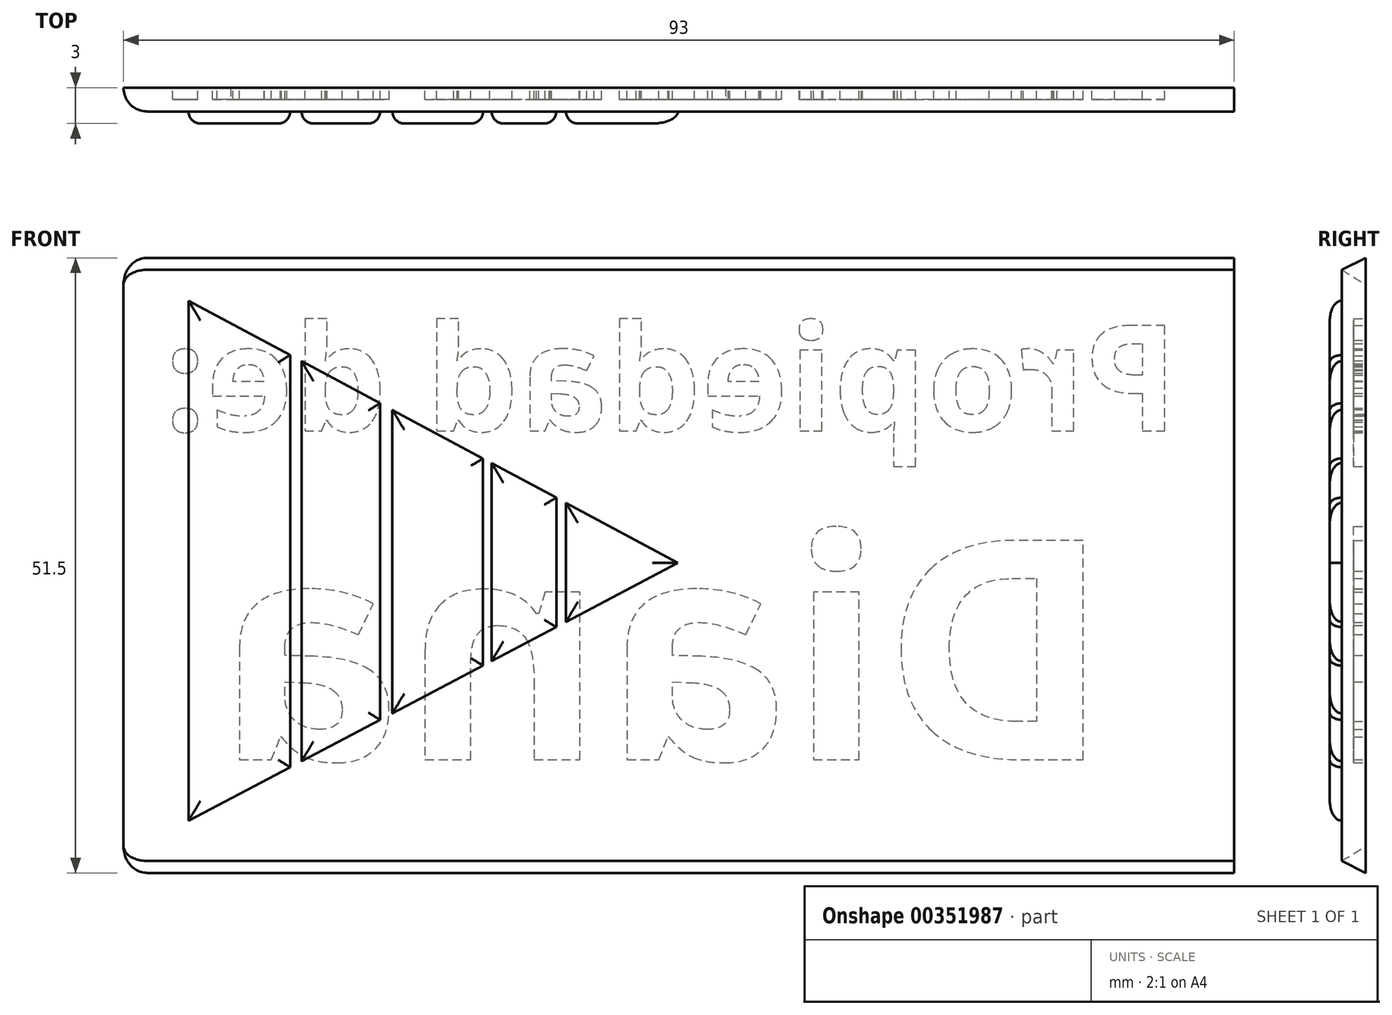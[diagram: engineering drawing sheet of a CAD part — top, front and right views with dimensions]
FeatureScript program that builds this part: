
annotation { "Feature Type Name" : "Feature", "Feature Type Description" : "" }
export const myFeature = defineFeature(function(context is Context, id is Id, definition is map)
    precondition{}
    {
        {
            var Q0;
            Q0=qCreatedBy(makeId("Front.planeOp"),FACE);
            var sketch = newSketch(context, id + "F0", { "sketchPlane" : qUnion([Q0])});
            skLineSegment(sketch, "E0", {"start": v(-25.75, -1) * mm, "end": v(25.75, -1) * mm});
            skLineSegment(sketch, "E1", {"start": v(-24.75, 1) * mm, "end": v(24.75, 1) * mm});
            skLineSegment(sketch, "E2", {"start": v(-24.75, 1) * mm, "end": v(-25.75, -1) * mm});
            skLineSegment(sketch, "E3", {"start": v(24.75, 1) * mm, "end": v(25.75, -1) * mm});
            skSolve(sketch);
        }
        {
            var Q0;
            Q0=makeQuery(id+"F0.imprint","IMPRINT",FACE,{"disambiguationData":[TD([[makeQuery(id+"F0.imprint","IMPRINT",EDGE,{"derivedFrom":sQuery(id+"F0.wireOp",EDGE,"E0")}),1.0]])]});
            extrude(context, id + "F1", {"entities" : qUnion([Q0]), "depth" : 93 * mm});
        }
        {
            var Q0;
            Q0=makeQuery(id+"F1.opExtrude","CAP_EDGE",EDGE,{"disambiguationData":[OSD([sQuery(id+"F0.wireOp",EDGE,"E1")])],"isStart":false});
            var Q1;
            Q1=makeQuery(id+"F1.opExtrude","CAP_EDGE",EDGE,{"disambiguationData":[OSD([sQuery(id+"F0.wireOp",EDGE,"E3")])],"isStart":false});
            var Q2;
            Q2=makeQuery(id+"F1.opExtrude","CAP_EDGE",EDGE,{"disambiguationData":[OSD([sQuery(id+"F0.wireOp",EDGE,"E2")])],"isStart":false});
            fillet(context, id + "F2", {"entities" : qUnion([Q0, Q1, Q2]), "radius" : 2 * mm, "tangentPropagation" : true, "allowEdgeOverflow" : false});
        }
        {
            var Q0;
            Q0=makeQuery(id+"F1.opExtrude","SWEPT_FACE",FACE,{"disambiguationData":[OSD([sQuery(id+"F0.wireOp",EDGE,"E1")])]});
            var sketch = newSketch(context, id + "F3", { "sketchPlane" : qUnion([Q0])});
            skLineSegment(sketch, "E4", {"start": v(-24.95, -92.76) * mm, "end": v(24.75, 0) * mm});
            skLineSegment(sketch, "E5", {"start": v(24.25, -93) * mm, "end": v(-24.75, 0) * mm});
            skLineSegment(sketch, "E6", {"start": v(-5.23, -55.95) * mm, "end": v(4.73, -55.95) * mm});
            skLineSegment(sketch, "E7", {"start": v(4.73, -55.95) * mm, "end": v(5.16, -56.76) * mm});
            skLineSegment(sketch, "E8", {"start": v(-5.67, -56.76) * mm, "end": v(5.16, -56.76) * mm});
            skLineSegment(sketch, "E9", {"start": v(-8.57, -62.18) * mm, "end": v(8.01, -62.18) * mm});
            skLineSegment(sketch, "E10", {"start": v(8.01, -62.18) * mm, "end": v(8.39, -62.9) * mm});
            skLineSegment(sketch, "E11", {"start": v(8.39, -62.9) * mm, "end": v(-8.95, -62.9) * mm});
            skLineSegment(sketch, "E12", {"start": v(-8.95, -62.9) * mm, "end": v(-13.02, -70.48) * mm});
            skLineSegment(sketch, "E13", {"start": v(-13.02, -70.48) * mm, "end": v(12.39, -70.48) * mm});
            skLineSegment(sketch, "E14", {"start": v(-13.57, -71.51) * mm, "end": v(12.93, -71.51) * mm});
            skLineSegment(sketch, "E15", {"start": v(16.4, -78.1) * mm, "end": v(-17.1, -78.1) * mm});
            skLineSegment(sketch, "E16", {"start": v(-17.6, -79.04) * mm, "end": v(16.9, -79.04) * mm});
            skLineSegment(sketch, "E17", {"start": v(-22.16, -87.55) * mm, "end": v(21.38, -87.55) * mm});
            skSolve(sketch);
        }
        {
            var Q0;
            {var subQ0=sQuery(id+"F3.wireOp",EDGE,"E6");Q0=makeQuery(id+"F3.imprint","IMPRINT",FACE,{"disambiguationData":[TD([[makeQuery(id+"F3.imprint","IMPRINT",EDGE,{"derivedFrom":subQ0}),1.0]])]});}
            var Q1;
            {var subQ0=sQuery(id+"F3.wireOp",EDGE,"E8");Q1=makeQuery(id+"F3.imprint","IMPRINT",FACE,{"disambiguationData":[TD([[makeQuery(id+"F3.imprint","IMPRINT",EDGE,{"derivedFrom":subQ0}),-1.0]])]});}
            var Q2;
            {var subQ0=sQuery(id+"F3.wireOp",EDGE,"E11");Q2=makeQuery(id+"F3.imprint","IMPRINT",FACE,{"disambiguationData":[TD([[makeQuery(id+"F3.imprint","IMPRINT",EDGE,{"derivedFrom":subQ0}),1.0]])]});}
            var Q3;
            {var subQ0=sQuery(id+"F3.wireOp",EDGE,"E14");Q3=makeQuery(id+"F3.imprint","IMPRINT",FACE,{"disambiguationData":[TD([[makeQuery(id+"F3.imprint","IMPRINT",EDGE,{"derivedFrom":subQ0}),-1.0]])]});}
            var Q4;
            {var subQ0=sQuery(id+"F3.wireOp",EDGE,"E16");Q4=makeQuery(id+"F3.imprint","IMPRINT",FACE,{"disambiguationData":[TD([[makeQuery(id+"F3.imprint","IMPRINT",EDGE,{"derivedFrom":subQ0}),-1.0]])]});}
            extrude(context, id + "F4", {"entities" : qUnion([Q0, Q1, Q2, Q3, Q4]), "operationType" : NewBodyOperationType.ADD, "depth" : 1 * mm});
        }
        {
            var Q0;
            Q0=makeQuery(id+"F4.opExtrude","CAP_FACE",FACE,{"disambiguationData":[OSD([sQuery(id+"F3.wireOp",EDGE,"E4"),sQuery(id+"F3.wireOp",EDGE,"E5"),sQuery(id+"F3.wireOp",EDGE,"E6")])],"isStart":false});
            var Q1;
            Q1=makeQuery(id+"F4.opExtrude","CAP_FACE",FACE,{"disambiguationData":[OSD([sQuery(id+"F3.wireOp",EDGE,"E4"),sQuery(id+"F3.wireOp",EDGE,"E5"),sQuery(id+"F3.wireOp",EDGE,"E8"),sQuery(id+"F3.wireOp",EDGE,"E9")])],"isStart":false});
            var Q2;
            Q2=makeQuery(id+"F4.opExtrude","CAP_FACE",FACE,{"disambiguationData":[OSD([sQuery(id+"F3.wireOp",EDGE,"E5"),sQuery(id+"F3.wireOp",EDGE,"E11"),sQuery(id+"F3.wireOp",EDGE,"E12"),sQuery(id+"F3.wireOp",EDGE,"E13")])],"isStart":false});
            var Q3;
            Q3=makeQuery(id+"F4.opExtrude","CAP_FACE",FACE,{"disambiguationData":[OSD([sQuery(id+"F3.wireOp",EDGE,"E4"),sQuery(id+"F3.wireOp",EDGE,"E5"),sQuery(id+"F3.wireOp",EDGE,"E16"),sQuery(id+"F3.wireOp",EDGE,"E17")])],"isStart":false});
            var Q4;
            Q4=makeQuery(id+"F4.opExtrude","CAP_FACE",FACE,{"disambiguationData":[OSD([sQuery(id+"F3.wireOp",EDGE,"E4"),sQuery(id+"F3.wireOp",EDGE,"E5"),sQuery(id+"F3.wireOp",EDGE,"E14"),sQuery(id+"F3.wireOp",EDGE,"E15")])],"isStart":false});
            fillet(context, id + "F5", {"entities" : qUnion([Q0, Q1, Q2, Q3, Q4]), "radius" : 1 * mm, "tangentPropagation" : true, "allowEdgeOverflow" : false});
        }
        {
            var Q0;
            Q0=makeQuery(id+"F1.opExtrude","SWEPT_BODY",BODY,{"disambiguationData":[OSD([sQuery(id+"F0.wireOp",EDGE,"E0"),sQuery(id+"F0.wireOp",EDGE,"E1"),sQuery(id+"F0.wireOp",EDGE,"E2"),sQuery(id+"F0.wireOp",EDGE,"E3")])]});
            var Q1;
            Q1=makeQuery(id+"F1.opExtrude","SWEPT_EDGE",EDGE,{"disambiguationData":[OSD([sQuery(id+"F0.wireOp",EDGE,"E0"),sQuery(id+"F0.wireOp",EDGE,"E2")])]});
            transform(context, id + "F6", {"entities" : qUnion([Q0]), "transformType" : TransformType.ROTATION, "transformAxis" : qUnion([Q1]), "angle" : 90 * degree, "makeCopy" : false});
        }
        {
            var Q0;
            Q0=makeQuery(id+"F1.opExtrude","SWEPT_BODY",BODY,{"disambiguationData":[OSD([sQuery(id+"F0.wireOp",EDGE,"E0"),sQuery(id+"F0.wireOp",EDGE,"E1"),sQuery(id+"F0.wireOp",EDGE,"E2"),sQuery(id+"F0.wireOp",EDGE,"E3")])]});
            var Q1;
            Q1=makeQuery(id+"F1.opExtrude","CAP_EDGE",EDGE,{"disambiguationData":[OSD([sQuery(id+"F0.wireOp",EDGE,"E1")])],"isStart":true});
            transform(context, id + "F7", {"entities" : qUnion([Q0]), "transformType" : TransformType.ROTATION, "transformAxis" : qUnion([Q1]), "angle" : 90 * degree, "makeCopy" : false});
        }
        {
            var Q0;
            Q0=makeQuery(id+"F1.opExtrude","SWEPT_FACE",FACE,{"disambiguationData":[OSD([sQuery(id+"F0.wireOp",EDGE,"E0")])]});
            var sketch = newSketch(context, id + "F8", { "sketchPlane" : qUnion([Q0])});
            skText(sketch, "E18", { "text": "Propiedad de:", "fontName": "OpenSans-Bold.ttf"});
            skText(sketch, "E19", { "text": "Diana", "fontName": "OpenSans-Bold.ttf"});
            const initialGuessF8  = {"E18": [0.02845, -0.01549, 1, 0, 0.0089], "E19": [0.0341, -0.04303, 1, 0, 0.01852]};
            skSetInitialGuess(sketch, initialGuessF8);
            skSolve(sketch);
        }
        {
            var Q0;
            Q0=makeQuery(id+"F8.imprint","IMPRINT",FACE,{"disambiguationData":[TD([[makeQuery(id+"F8.imprint","IMPRINT",EDGE,{"derivedFrom":sQuery(id+"F8.wireOp",EDGE,"E19.sketch_text.stroke-17")}),-1.0]])]});
            var Q1;
            Q1=makeQuery(id+"F8.imprint","IMPRINT",FACE,{"disambiguationData":[TD([[makeQuery(id+"F8.imprint","IMPRINT",EDGE,{"derivedFrom":sQuery(id+"F8.wireOp",EDGE,"E19.sketch_text.stroke-12")}),-1.0]])]});
            var Q2;
            Q2=makeQuery(id+"F8.imprint","IMPRINT",FACE,{"disambiguationData":[TD([[makeQuery(id+"F8.imprint","IMPRINT",EDGE,{"derivedFrom":sQuery(id+"F8.wireOp",EDGE,"E19.sketch_text.stroke-21")}),-1.0]])]});
            var Q3;
            Q3=makeQuery(id+"F8.imprint","IMPRINT",FACE,{"disambiguationData":[TD([[makeQuery(id+"F8.imprint","IMPRINT",EDGE,{"derivedFrom":sQuery(id+"F8.wireOp",EDGE,"E19.sketch_text.stroke-46")}),-1.0]])]});
            var Q4;
            Q4=makeQuery(id+"F8.imprint","IMPRINT",FACE,{"disambiguationData":[TD([[makeQuery(id+"F8.imprint","IMPRINT",EDGE,{"derivedFrom":sQuery(id+"F8.wireOp",EDGE,"E19.sketch_text.stroke-63")}),-1.0]])]});
            var Q5;
            Q5=makeQuery(id+"F8.imprint","IMPRINT",FACE,{"disambiguationData":[TD([[makeQuery(id+"F8.imprint","IMPRINT",EDGE,{"derivedFrom":sQuery(id+"F8.wireOp",EDGE,"E18.sketch_text.stroke-213")}),-1.0]])]});
            var Q6;
            Q6=makeQuery(id+"F8.imprint","IMPRINT",FACE,{"disambiguationData":[TD([[makeQuery(id+"F8.imprint","IMPRINT",EDGE,{"derivedFrom":sQuery(id+"F8.wireOp",EDGE,"E18.sketch_text.stroke-221")}),-1.0]])]});
            var Q7;
            Q7=makeQuery(id+"F8.imprint","IMPRINT",FACE,{"disambiguationData":[TD([[makeQuery(id+"F8.imprint","IMPRINT",EDGE,{"derivedFrom":sQuery(id+"F8.wireOp",EDGE,"E18.sketch_text.stroke-193")}),-1.0]])]});
            var Q8;
            Q8=makeQuery(id+"F8.imprint","IMPRINT",FACE,{"disambiguationData":[TD([[makeQuery(id+"F8.imprint","IMPRINT",EDGE,{"derivedFrom":sQuery(id+"F8.wireOp",EDGE,"E18.sketch_text.stroke-170")}),-1.0]])]});
            var Q9;
            Q9=makeQuery(id+"F8.imprint","IMPRINT",FACE,{"disambiguationData":[TD([[makeQuery(id+"F8.imprint","IMPRINT",EDGE,{"derivedFrom":sQuery(id+"F8.wireOp",EDGE,"E18.sketch_text.stroke-147")}),-1.0]])]});
            var Q10;
            Q10=makeQuery(id+"F8.imprint","IMPRINT",FACE,{"disambiguationData":[TD([[makeQuery(id+"F8.imprint","IMPRINT",EDGE,{"derivedFrom":sQuery(id+"F8.wireOp",EDGE,"E18.sketch_text.stroke-122")}),-1.0]])]});
            var Q11;
            Q11=makeQuery(id+"F8.imprint","IMPRINT",FACE,{"disambiguationData":[TD([[makeQuery(id+"F8.imprint","IMPRINT",EDGE,{"derivedFrom":sQuery(id+"F8.wireOp",EDGE,"E18.sketch_text.stroke-99")}),-1.0]])]});
            var Q12;
            Q12=makeQuery(id+"F8.imprint","IMPRINT",FACE,{"disambiguationData":[TD([[makeQuery(id+"F8.imprint","IMPRINT",EDGE,{"derivedFrom":sQuery(id+"F8.wireOp",EDGE,"E19.sketch_text.stroke-0")}),-1.0]])]});
            var Q13;
            Q13=makeQuery(id+"F8.imprint","IMPRINT",FACE,{"disambiguationData":[TD([[makeQuery(id+"F8.imprint","IMPRINT",EDGE,{"derivedFrom":sQuery(id+"F8.wireOp",EDGE,"E18.sketch_text.stroke-79")}),-1.0]])]});
            var Q14;
            Q14=makeQuery(id+"F8.imprint","IMPRINT",FACE,{"disambiguationData":[TD([[makeQuery(id+"F8.imprint","IMPRINT",EDGE,{"derivedFrom":sQuery(id+"F8.wireOp",EDGE,"E18.sketch_text.stroke-75")}),-1.0]])]});
            var Q15;
            Q15=makeQuery(id+"F8.imprint","IMPRINT",FACE,{"disambiguationData":[TD([[makeQuery(id+"F8.imprint","IMPRINT",EDGE,{"derivedFrom":sQuery(id+"F8.wireOp",EDGE,"E18.sketch_text.stroke-70")}),-1.0]])]});
            var Q16;
            Q16=makeQuery(id+"F8.imprint","IMPRINT",FACE,{"disambiguationData":[TD([[makeQuery(id+"F8.imprint","IMPRINT",EDGE,{"derivedFrom":sQuery(id+"F8.wireOp",EDGE,"E18.sketch_text.stroke-47")}),-1.0]])]});
            var Q17;
            Q17=makeQuery(id+"F8.imprint","IMPRINT",FACE,{"disambiguationData":[TD([[makeQuery(id+"F8.imprint","IMPRINT",EDGE,{"derivedFrom":sQuery(id+"F8.wireOp",EDGE,"E18.sketch_text.stroke-29")}),-1.0]])]});
            var Q18;
            Q18=makeQuery(id+"F8.imprint","IMPRINT",FACE,{"disambiguationData":[TD([[makeQuery(id+"F8.imprint","IMPRINT",EDGE,{"derivedFrom":sQuery(id+"F8.wireOp",EDGE,"E18.sketch_text.stroke-16")}),-1.0]])]});
            var Q19;
            Q19=makeQuery(id+"F8.imprint","IMPRINT",FACE,{"disambiguationData":[TD([[makeQuery(id+"F8.imprint","IMPRINT",EDGE,{"derivedFrom":sQuery(id+"F8.wireOp",EDGE,"E18.sketch_text.stroke-0")}),-1.0]])]});
            extrude(context, id + "F9", {"entities" : qUnion([Q0, Q1, Q2, Q3, Q4, Q5, Q6, Q7, Q8, Q9, Q10, Q11, Q12, Q13, Q14, Q15, Q16, Q17, Q18, Q19]), "operationType" : NewBodyOperationType.REMOVE, "oppositeDirection" : true, "depth" : 1 * mm});
        }
    });
